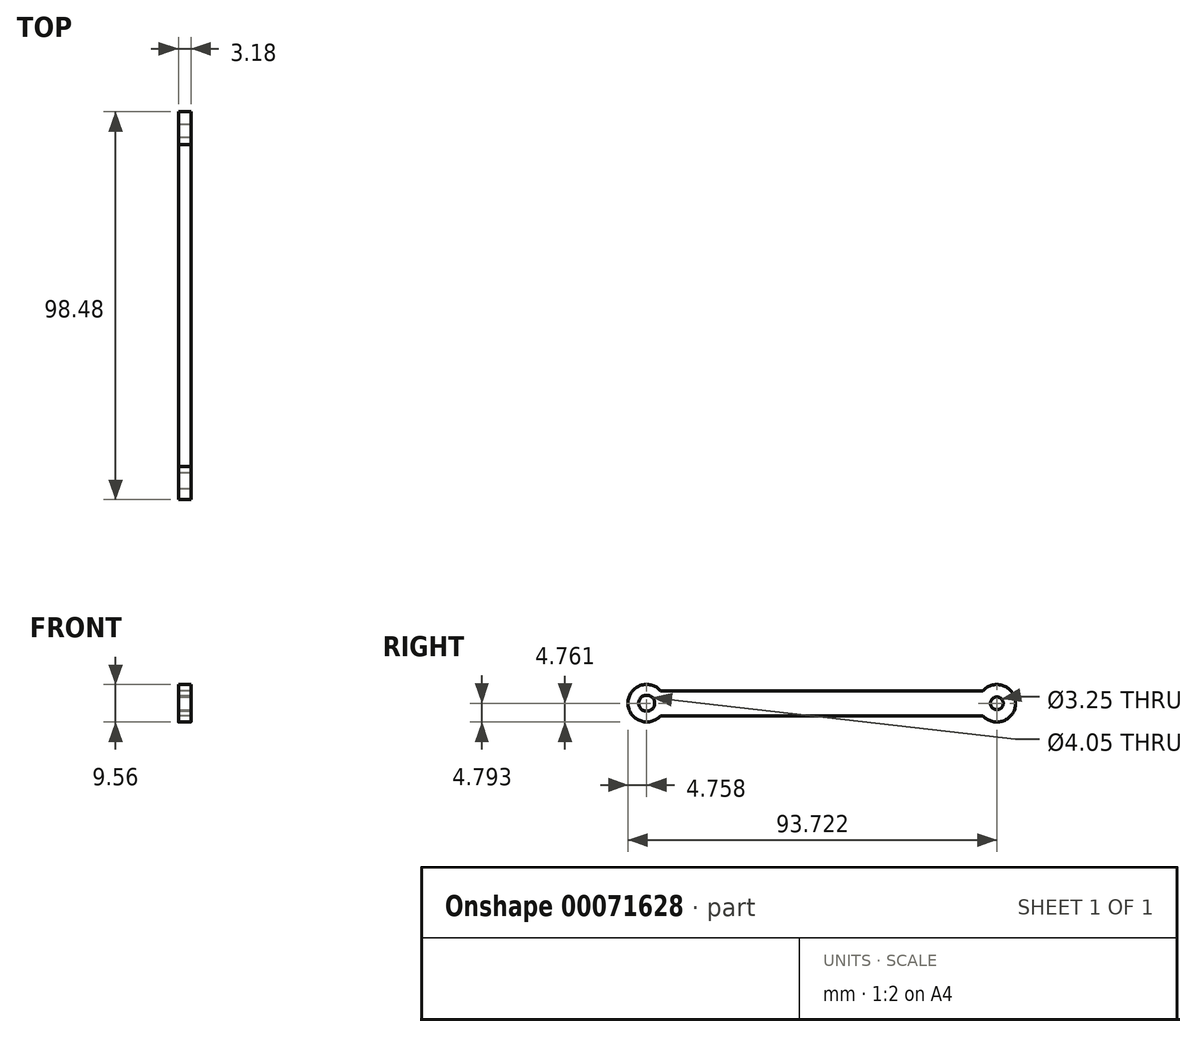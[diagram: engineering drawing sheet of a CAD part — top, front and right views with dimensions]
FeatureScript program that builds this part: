
annotation { "Feature Type Name" : "Feature", "Feature Type Description" : "" }
export const myFeature = defineFeature(function(context is Context, id is Id, definition is map)
    precondition{}
    {
        {
            var Q0;
            Q0=qCreatedBy(makeId("Right.planeOp"),FACE);
            var sketch = newSketch(context, id + "F0", { "sketchPlane" : qUnion([Q0])});
            skLineSegment(sketch, "E0.bottom", {"start": v(-54.64, 20.68) * mm, "end": v(34.26, 20.68) * mm});
            skLineSegment(sketch, "E0.top", {"start": v(-54.64, 14.33) * mm, "end": v(34.26, 14.33) * mm});
            skLineSegment(sketch, "E0.left", {"start": v(-54.64, 20.68) * mm, "end": v(-54.64, 14.33) * mm});
            skLineSegment(sketch, "E0.right", {"start": v(34.26, 20.68) * mm, "end": v(34.26, 14.33) * mm});
            skSolve(sketch);
        }
        {
            var Q0;
            Q0 = qSketchRegion(id + "F0", true);
            extrude(context, id + "F1", {"entities" : qUnion([Q0]), "depth" : 3.17 * mm});
        }
        {
            var Q0;
            Q0=qCreatedBy(makeId("Right.planeOp"),FACE);
            var sketch = newSketch(context, id + "F2", { "sketchPlane" : qUnion([Q0])});
            skLineSegment(sketch, "E1", {"start": v(-54.66, 14.35) * mm, "end": v(-54.66, 20.7) * mm});
            skCircle(sketch, "E2", {"center": v(-54.66, 17.52) * mm, "radius": 4.76 * mm});
            skSolve(sketch);
        }
        {
            var Q0;
            Q0 = qSketchRegion(id + "F2", true);
            extrude(context, id + "F3", {"entities" : qUnion([Q0]), "operationType" : NewBodyOperationType.ADD, "depth" : 3.17 * mm});
        }
        {
            var Q0;
            Q0=qCreatedBy(makeId("Right.planeOp"),FACE);
            var sketch = newSketch(context, id + "F4", { "sketchPlane" : qUnion([Q0])});
            skLineSegment(sketch, "E3", {"start": v(34.3, 20.67) * mm, "end": v(34.3, 14.32) * mm});
            skCircle(sketch, "E4", {"center": v(34.3, 17.5) * mm, "radius": 4.76 * mm});
            skSolve(sketch);
        }
        {
            var Q0;
            Q0 = qSketchRegion(id + "F4", true);
            extrude(context, id + "F5", {"entities" : qUnion([Q0]), "operationType" : NewBodyOperationType.ADD, "depth" : 3.17 * mm});
        }
        {
            var Q0;
            Q0=makeQuery(id+"F5.boolean.opBoolean","MERGE",FACE,{"derivedFrom":[makeQuery(id+"F3.boolean.opBoolean","MERGE",FACE,{"derivedFrom":[makeQuery(id+"F1.opExtrude","CAP_FACE",FACE,{"disambiguationData":[OSD([sQuery(id+"F0.wireOp",EDGE,"E0.bottom"),sQuery(id+"F0.wireOp",EDGE,"E0.top"),sQuery(id+"F0.wireOp",EDGE,"E0.left"),sQuery(id+"F0.wireOp",EDGE,"E0.right")])],"isStart":false}),makeQuery(id+"F3.opExtrude","CAP_FACE",FACE,{"disambiguationData":[OSD([sQuery(id+"F2.wireOp",EDGE,"E2")])],"isStart":false})]}),makeQuery(id+"F5.opExtrude","CAP_FACE",FACE,{"disambiguationData":[OSD([sQuery(id+"F4.wireOp",EDGE,"E4")])],"isStart":false})]});
            var sketch = newSketch(context, id + "F6", { "sketchPlane" : qUnion([Q0])});
            skCircle(sketch, "E5", {"center": v(-54.66, 17.52) * mm, "radius": 2.02 * mm});
            skCircle(sketch, "E6", {"center": v(34.3, 17.5) * mm, "radius": 1.63 * mm});
            skSolve(sketch);
        }
        {
            var Q0;
            Q0 = qSketchRegion(id + "F6", true);
            extrude(context, id + "F7", {"entities" : qUnion([Q0]), "operationType" : NewBodyOperationType.REMOVE, "oppositeDirection" : true, "depth" : 3.17 * mm});
        }
    });
